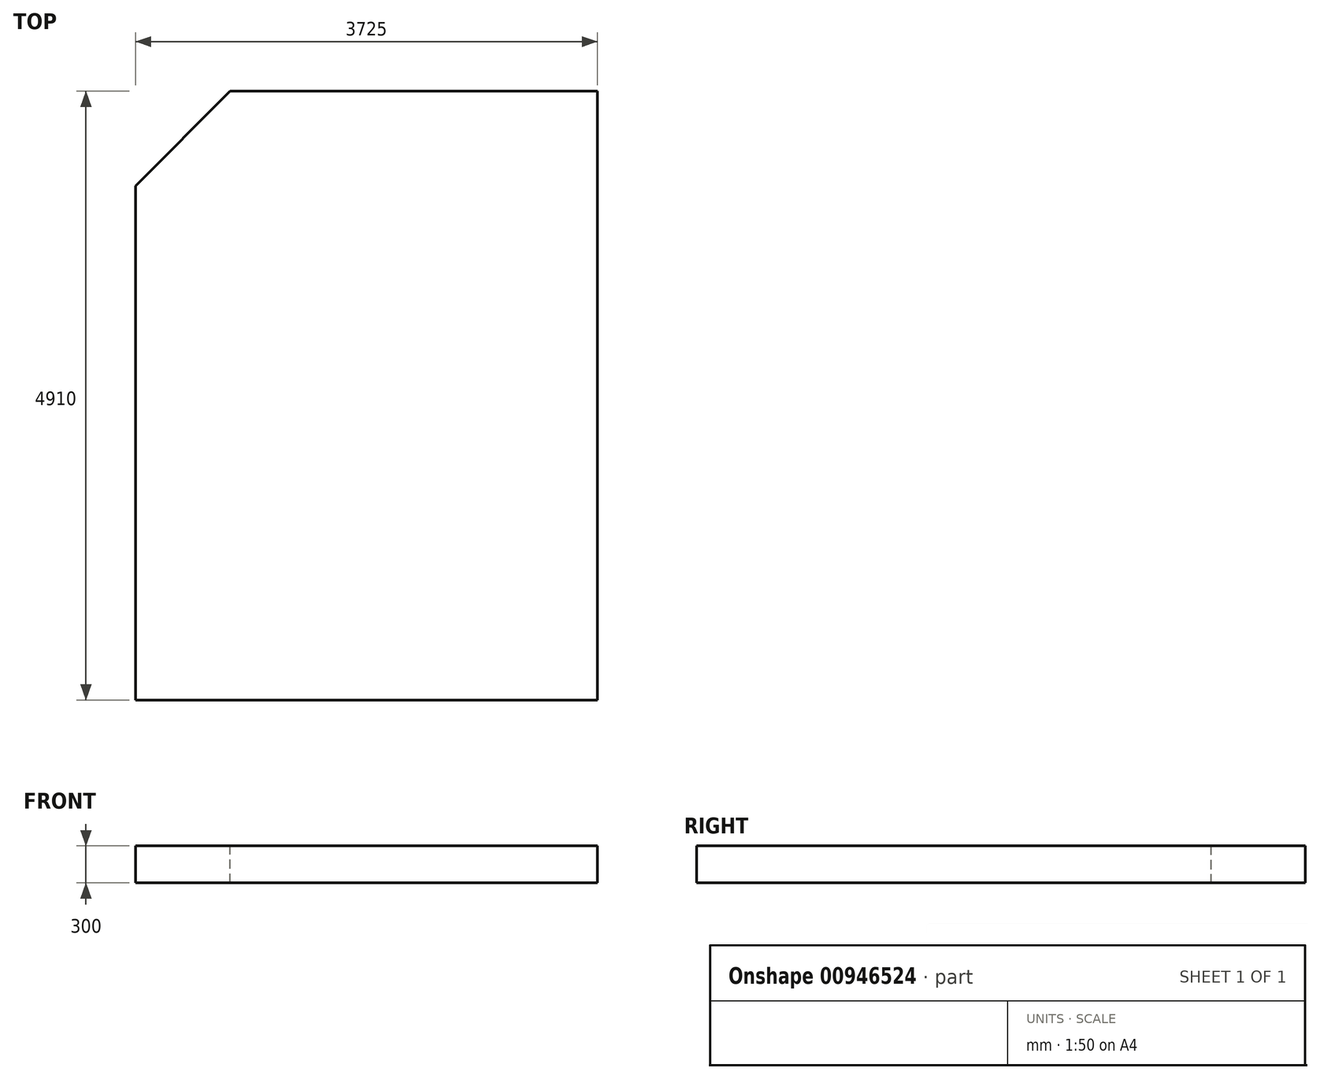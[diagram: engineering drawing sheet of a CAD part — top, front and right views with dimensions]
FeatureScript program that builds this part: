
annotation { "Feature Type Name" : "Feature", "Feature Type Description" : "" }
export const myFeature = defineFeature(function(context is Context, id is Id, definition is map)
    precondition{}
    {
        {
            var Q0;
            Q0=qCreatedBy(makeId("Front.planeOp"),FACE);
            var sketch = newSketch(context, id + "F0", { "sketchPlane" : qUnion([Q0])});
            skLineSegment(sketch, "E0.bottom", {"start": v(0, 0) * mm, "end": v(-3725, 0) * mm});
            skLineSegment(sketch, "E0.top", {"start": v(0, 300) * mm, "end": v(-3725, 300) * mm});
            skLineSegment(sketch, "E0.left", {"start": v(0, 0) * mm, "end": v(0, 300) * mm});
            skLineSegment(sketch, "E0.right", {"start": v(-3725, 0) * mm, "end": v(-3725, 300) * mm});
            skSolve(sketch);
        }
        {
            var Q0;
            Q0 = qSketchRegion(id + "F0", true);
            extrude(context, id + "F1", {"entities" : qUnion([Q0]), "depth" : 4910 * mm, "offsetDistance" : 25 * mm});
        }
        {
            var Q0;
            Q0=makeQuery(id+"F1.opExtrude","CAP_EDGE",EDGE,{"disambiguationData":[OSD([sQuery(id+"F0.wireOp",EDGE,"E0.right")])],"isStart":true});
            chamfer(context, id + "F2", {"entities" : qUnion([Q0]), "width" : 763 * mm, "tangentPropagation" : true});
        }
    });
